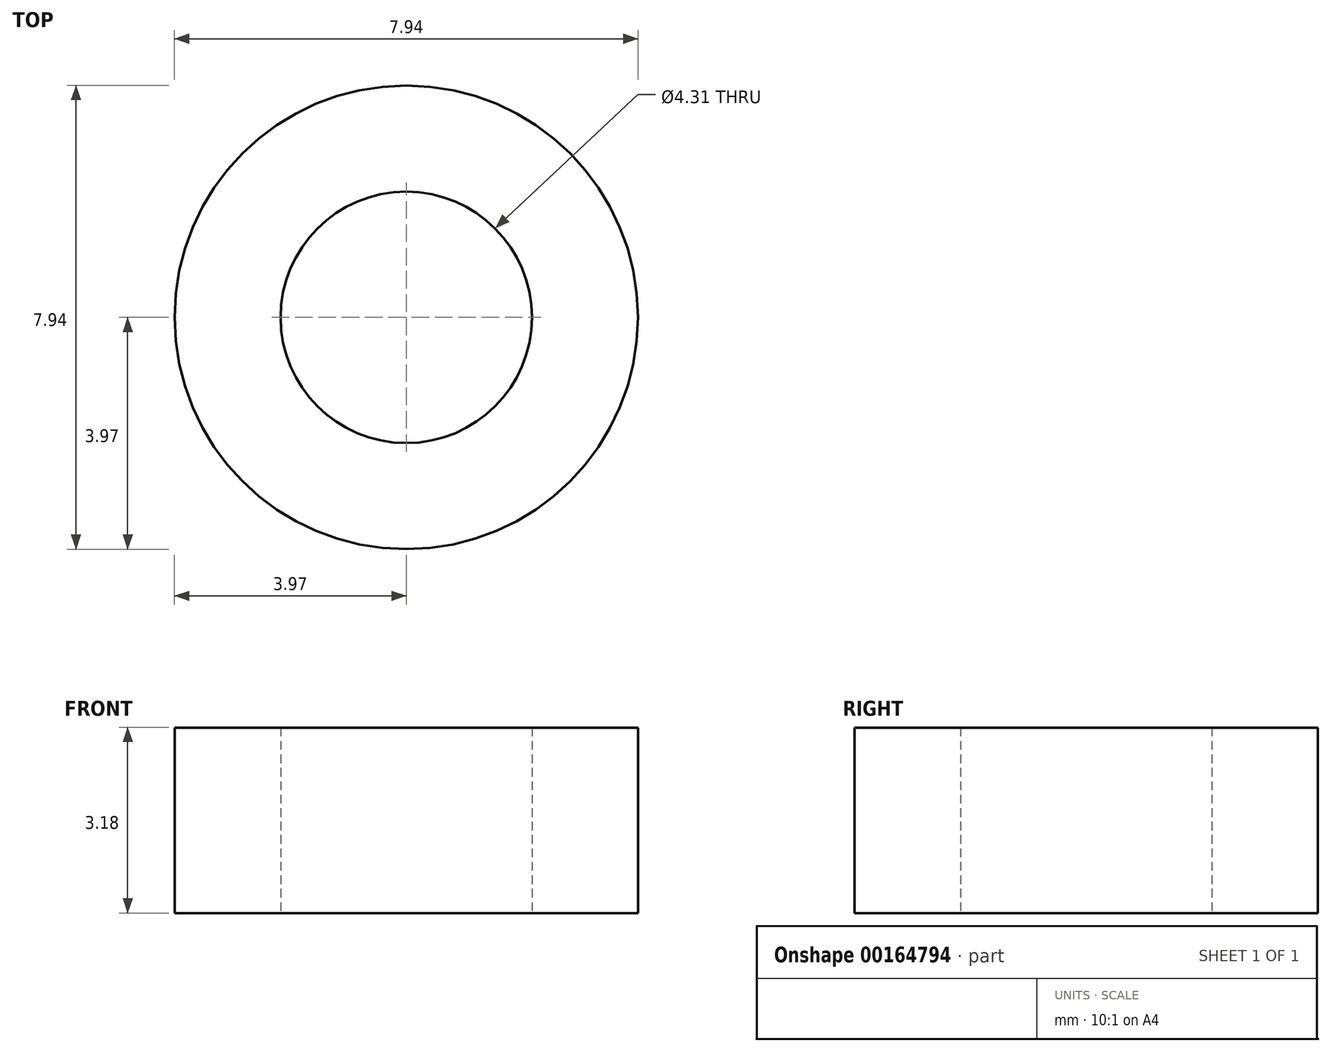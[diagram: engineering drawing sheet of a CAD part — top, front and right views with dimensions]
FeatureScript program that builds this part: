
annotation { "Feature Type Name" : "Feature", "Feature Type Description" : "" }
export const myFeature = defineFeature(function(context is Context, id is Id, definition is map)
    precondition{}
    {
        {
            var Q0;
            Q0=qCreatedBy(makeId("Top.planeOp"),FACE);
            var sketch = newSketch(context, id + "F0", { "sketchPlane" : qUnion([Q0])});
            skCircle(sketch, "E0", {"center": v(0, 0) * mm, "radius": 2.15 * mm});
            skCircle(sketch, "E1", {"center": v(0, 0) * mm, "radius": 3.97 * mm});
            skSolve(sketch);
        }
        {
            var Q0;
            Q0 = qSketchRegion(id + "F0", true);
            extrude(context, id + "F1", {"entities" : qUnion([Q0]), "depth" : 3.17 * mm});
        }
    });
